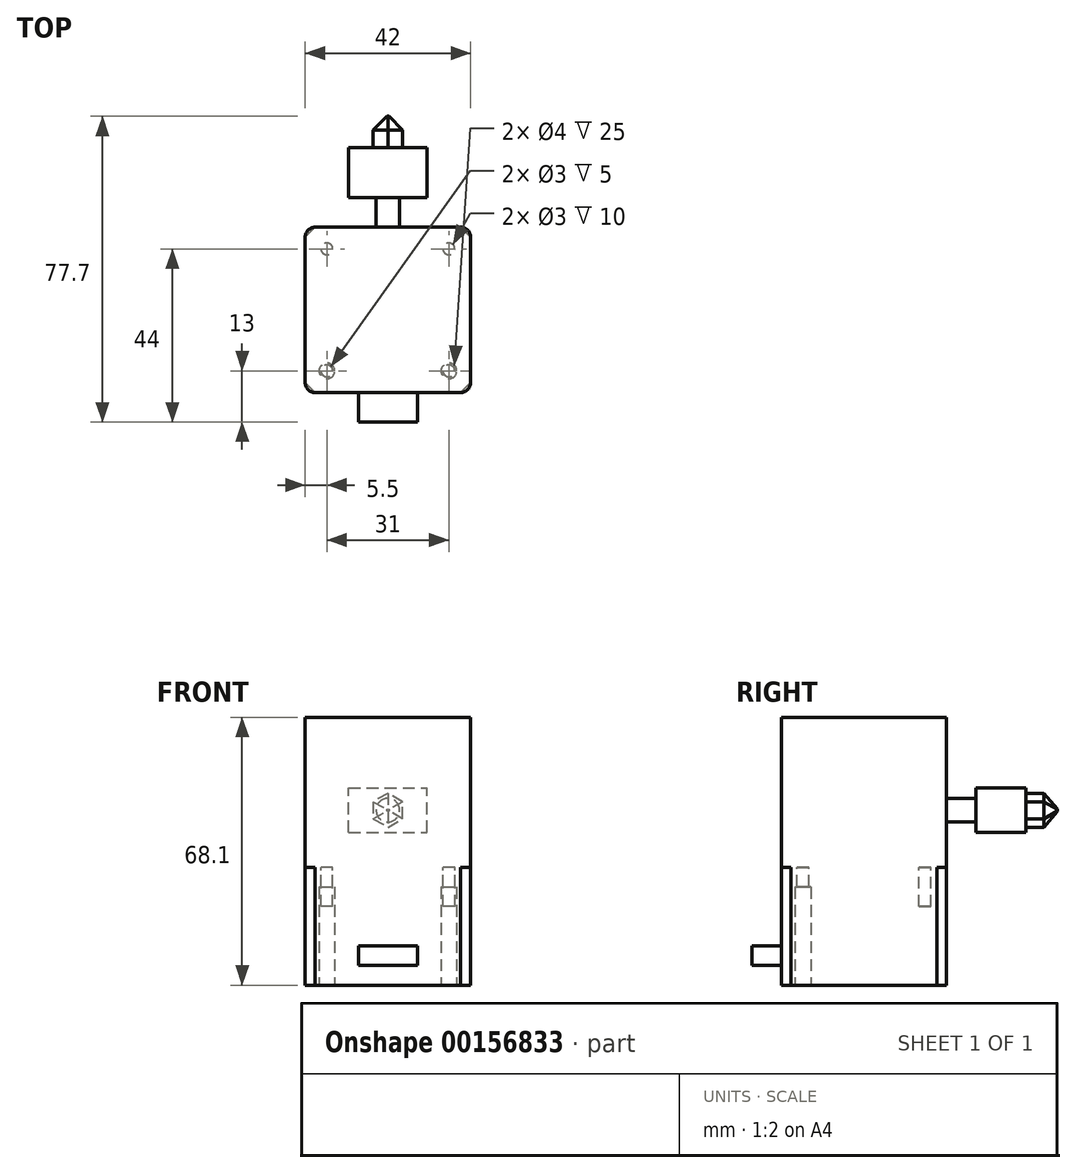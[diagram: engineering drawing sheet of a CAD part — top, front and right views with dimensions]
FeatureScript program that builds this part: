
annotation { "Feature Type Name" : "Feature", "Feature Type Description" : "" }
export const myFeature = defineFeature(function(context is Context, id is Id, definition is map)
    precondition{}
    {
        {
            var Q0;
            Q0=qCreatedBy(makeId("Top.planeOp"),FACE);
            var sketch = newSketch(context, id + "F0", { "sketchPlane" : qUnion([Q0])});
            skLineSegment(sketch, "E0.bottom", {"start": v(21, -21) * mm, "end": v(-21, -21) * mm});
            skLineSegment(sketch, "E0.top", {"start": v(21, 21) * mm, "end": v(-21, 21) * mm});
            skLineSegment(sketch, "E0.left", {"start": v(21, -21) * mm, "end": v(21, 21) * mm});
            skLineSegment(sketch, "E0.right", {"start": v(-21, -21) * mm, "end": v(-21, 21) * mm});
            skPoint(sketch, "E0.middle", {"position": v(0, 0) * mm});
            skSolve(sketch);
        }
        {
            var Q0;
            Q0=qSketchRegion(id+"F0",true);
            extrude(context, id + "F1", {"entities" : qUnion([Q0]), "depth" : 30 * mm});
        }
        {
            var Q0;
            Q0=makeQuery(id+"F1.opExtrude","SWEPT_EDGE",EDGE,{"disambiguationData":[OSD([sQuery(id+"F0.wireOp",EDGE,"E0.bottom"),sQuery(id+"F0.wireOp",EDGE,"E0.right")])]});
            var Q1;
            Q1=makeQuery(id+"F1.opExtrude","SWEPT_EDGE",EDGE,{"disambiguationData":[OSD([sQuery(id+"F0.wireOp",EDGE,"E0.bottom"),sQuery(id+"F0.wireOp",EDGE,"E0.left")])]});
            var Q2;
            Q2=makeQuery(id+"F1.opExtrude","SWEPT_EDGE",EDGE,{"disambiguationData":[OSD([sQuery(id+"F0.wireOp",EDGE,"E0.top"),sQuery(id+"F0.wireOp",EDGE,"E0.left")])]});
            var Q3;
            Q3=makeQuery(id+"F1.opExtrude","SWEPT_EDGE",EDGE,{"disambiguationData":[OSD([sQuery(id+"F0.wireOp",EDGE,"E0.top"),sQuery(id+"F0.wireOp",EDGE,"E0.right")])]});
            chamfer(context, id + "F2", {"entities" : qUnion([Q0, Q1, Q2, Q3]), "width" : 2.5 * mm, "tangentPropagation" : true});
        }
        {
            var Q0;
            Q0=makeQuery(id+"F1.opExtrude","CAP_FACE",FACE,{"disambiguationData":[OSD([sQuery(id+"F0.wireOp",EDGE,"E0.bottom"),sQuery(id+"F0.wireOp",EDGE,"E0.top"),sQuery(id+"F0.wireOp",EDGE,"E0.left"),sQuery(id+"F0.wireOp",EDGE,"E0.right")])],"isStart":false});
            var sketch = newSketch(context, id + "F3", { "sketchPlane" : qUnion([Q0])});
            skLineSegment(sketch, "E1.bottom", {"start": v(15.5, -15.5) * mm, "end": v(-15.5, -15.5) * mm, "construction": true});
            skLineSegment(sketch, "E1.top", {"start": v(15.5, 15.5) * mm, "end": v(-15.5, 15.5) * mm, "construction": true});
            skLineSegment(sketch, "E1.left", {"start": v(15.5, -15.5) * mm, "end": v(15.5, 15.5) * mm, "construction": true});
            skLineSegment(sketch, "E1.right", {"start": v(-15.5, -15.5) * mm, "end": v(-15.5, 15.5) * mm, "construction": true});
            skPoint(sketch, "E1.middle", {"position": v(0, 0) * mm});
            skCircle(sketch, "E2", {"center": v(-15.5, 15.5) * mm, "radius": 1.5 * mm});
            skCircle(sketch, "E3", {"center": v(15.5, 15.5) * mm, "radius": 1.5 * mm});
            skCircle(sketch, "E4", {"center": v(15.5, -15.5) * mm, "radius": 1.5 * mm});
            skCircle(sketch, "E5", {"center": v(-15.5, -15.5) * mm, "radius": 1.5 * mm});
            skSolve(sketch);
        }
        {
            var Q0;
            Q0=qSketchRegion(id+"F3",true);
            extrude(context, id + "F4", {"entities" : qUnion([Q0]), "operationType" : NewBodyOperationType.REMOVE, "oppositeDirection" : true, "depth" : 10 * mm});
        }
        {
            var Q0;
            Q0=makeQuery(id+"F1.opExtrude","CAP_FACE",FACE,{"disambiguationData":[OSD([sQuery(id+"F0.wireOp",EDGE,"E0.bottom"),sQuery(id+"F0.wireOp",EDGE,"E0.top"),sQuery(id+"F0.wireOp",EDGE,"E0.left"),sQuery(id+"F0.wireOp",EDGE,"E0.right")])],"isStart":false});
            var sketch = newSketch(context, id + "F5", { "sketchPlane" : qUnion([Q0])});
            skCircle(sketch, "E6", {"center": v(0, 0) * mm, "radius": 11 * mm});
            skSolve(sketch);
        }
        {
            var Q0;
            Q0=qSketchRegion(id+"F5",true);
            extrude(context, id + "F6", {"entities" : qUnion([Q0]), "operationType" : NewBodyOperationType.ADD, "depth" : 2 * mm});
        }
        {
            var Q0;
            Q0=makeQuery(id+"F6.opExtrude","CAP_FACE",FACE,{"disambiguationData":[OSD([sQuery(id+"F5.wireOp",EDGE,"E6")])],"isStart":false});
            var sketch = newSketch(context, id + "F7", { "sketchPlane" : qUnion([Q0])});
            skArc(sketch, "E7", {"start": v(-2.2, 1.2) * mm, "mid": v(0, -2.5) * mm, "end": v(2.2, 1.2) * mm});
            skLineSegment(sketch, "E8", {"start": v(-2.2, 1.2) * mm, "end": v(2.2, 1.2) * mm});
            skSolve(sketch);
        }
        {
            var Q0;
            Q0=qSketchRegion(id+"F7",true);
            extrude(context, id + "F8", {"entities" : qUnion([Q0]), "operationType" : NewBodyOperationType.ADD, "depth" : 24 * mm});
        }
        {
            var Q0;
            Q0=makeQuery(id+"F1.opExtrude","SWEPT_FACE",FACE,{"disambiguationData":[OSD([sQuery(id+"F0.wireOp",EDGE,"E0.bottom")])]});
            var sketch = newSketch(context, id + "F9", { "sketchPlane" : qUnion([Q0])});
            skLineSegment(sketch, "E9.bottom", {"start": v(7.5, 5) * mm, "end": v(-7.5, 5) * mm});
            skLineSegment(sketch, "E9.top", {"start": v(7.5, 10) * mm, "end": v(-7.5, 10) * mm});
            skLineSegment(sketch, "E9.left", {"start": v(7.5, 5) * mm, "end": v(7.5, 10) * mm});
            skLineSegment(sketch, "E9.right", {"start": v(-7.5, 5) * mm, "end": v(-7.5, 10) * mm});
            skPoint(sketch, "E9.middle", {"position": v(0, 7.5) * mm});
            skSolve(sketch);
        }
        {
            var Q0;
            Q0=qSketchRegion(id+"F9",true);
            extrude(context, id + "F10", {"entities" : qUnion([Q0]), "operationType" : NewBodyOperationType.ADD, "depth" : 7.5 * mm});
        }
        {
            var Q0;
            Q0=makeQuery(id+"F1.opExtrude","CAP_FACE",FACE,{"disambiguationData":[OSD([sQuery(id+"F0.wireOp",EDGE,"E0.bottom"),sQuery(id+"F0.wireOp",EDGE,"E0.top"),sQuery(id+"F0.wireOp",EDGE,"E0.left"),sQuery(id+"F0.wireOp",EDGE,"E0.right")])],"isStart":false});
            var sketch = newSketch(context, id + "F11", { "sketchPlane" : qUnion([Q0])});
            skLineSegment(sketch, "E10.bottom", {"start": v(18.5, -21) * mm, "end": v(-18.5, -21) * mm});
            skLineSegment(sketch, "E10.top", {"start": v(18.5, 21) * mm, "end": v(-18.5, 21) * mm});
            skLineSegment(sketch, "E10.left", {"start": v(21, -18.5) * mm, "end": v(21, 18.5) * mm});
            skLineSegment(sketch, "E10.right", {"start": v(-21, -18.5) * mm, "end": v(-21, 18.5) * mm});
            skPoint(sketch, "E10.middle", {"position": v(0, 0) * mm});
            skPoint(sketch, "E11.visualSharp", {"position": v(-21, 21) * mm});
            skArc(sketch, "E11.filletArc", {"start": v(-18.5, 21) * mm, "mid": v(-20.27, 20.27) * mm, "end": v(-21, 18.5) * mm});
            skPoint(sketch, "E12.visualSharp", {"position": v(21, 21) * mm});
            skArc(sketch, "E12.filletArc", {"start": v(21, 18.5) * mm, "mid": v(20.27, 20.27) * mm, "end": v(18.5, 21) * mm});
            skPoint(sketch, "E13.visualSharp", {"position": v(21, -21) * mm});
            skArc(sketch, "E13.filletArc", {"start": v(18.5, -21) * mm, "mid": v(20.27, -20.27) * mm, "end": v(21, -18.5) * mm});
            skPoint(sketch, "E14.visualSharp", {"position": v(-21, -21) * mm});
            skArc(sketch, "E14.filletArc", {"start": v(-21, -18.5) * mm, "mid": v(-20.27, -20.27) * mm, "end": v(-18.5, -21) * mm});
            skSolve(sketch);
        }
        {
            var Q0;
            Q0=qSketchRegion(id+"F11",true);
            extrude(context, id + "F12", {"entities" : qUnion([Q0]), "operationType" : NewBodyOperationType.ADD, "depth" : 38.1 * mm});
        }
        {
            var Q0;
            Q0=makeQuery(id+"F12.boolean.opBoolean","MERGE",FACE,{"derivedFrom":[makeQuery(id+"F1.opExtrude","SWEPT_FACE",FACE,{"disambiguationData":[OSD([sQuery(id+"F0.wireOp",EDGE,"E0.top")])]}),makeQuery(id+"F12.opExtrude","SWEPT_FACE",FACE,{"disambiguationData":[OSD([sQuery(id+"F11.wireOp",EDGE,"E10.top")])]})]});
            var sketch = newSketch(context, id + "F13", { "sketchPlane" : qUnion([Q0])});
            skCircle(sketch, "E15", {"center": v(0, 44.47) * mm, "radius": 3 * mm});
            skSolve(sketch);
        }
        {
            var Q0;
            Q0=qSketchRegion(id+"F13",true);
            extrude(context, id + "F14", {"entities" : qUnion([Q0]), "operationType" : NewBodyOperationType.ADD, "depth" : 7.5 * mm});
        }
        {
            var Q0;
            Q0=makeQuery(id+"F14.opExtrude","CAP_FACE",FACE,{"disambiguationData":[OSD([sQuery(id+"F13.wireOp",EDGE,"E15")])],"isStart":false});
            var sketch = newSketch(context, id + "F15", { "sketchPlane" : qUnion([Q0])});
            skLineSegment(sketch, "E16.bottom", {"start": v(10, 38.85) * mm, "end": v(-10, 38.85) * mm});
            skLineSegment(sketch, "E16.top", {"start": v(10, 50.1) * mm, "end": v(-10, 50.1) * mm});
            skLineSegment(sketch, "E16.left", {"start": v(10, 38.85) * mm, "end": v(10, 50.1) * mm});
            skLineSegment(sketch, "E16.right", {"start": v(-10, 38.85) * mm, "end": v(-10, 50.1) * mm});
            skPoint(sketch, "E16.middle", {"position": v(0, 44.47) * mm});
            skSolve(sketch);
        }
        {
            var Q0;
            Q0=qSketchRegion(id+"F15",true);
            extrude(context, id + "F16", {"entities" : qUnion([Q0]), "operationType" : NewBodyOperationType.ADD, "depth" : 12.7 * mm});
        }
        {
            var Q0;
            Q0=makeQuery(id+"F16.opExtrude","CAP_FACE",FACE,{"disambiguationData":[OSD([sQuery(id+"F15.wireOp",EDGE,"E16.bottom"),sQuery(id+"F15.wireOp",EDGE,"E16.top"),sQuery(id+"F15.wireOp",EDGE,"E16.left"),sQuery(id+"F15.wireOp",EDGE,"E16.right")])],"isStart":false});
            var sketch = newSketch(context, id + "F17", { "sketchPlane" : qUnion([Q0])});
            skCircle(sketch, "E17.cCircle", {"center": v(0, 44.47) * mm, "radius": 3.75 * mm, "construction": true});
            skPoint(sketch, "E17.cCircle.centerSnap0", {"position": v(0, 50.1) * mm});
            skLineSegment(sketch, "E17.0", {"start": v(3.75, 46.64) * mm, "end": v(3.75, 42.3) * mm});
            skLineSegment(sketch, "E17.1", {"start": v(3.75, 42.3) * mm, "end": v(0, 40.14) * mm});
            skLineSegment(sketch, "E17.2", {"start": v(0, 40.14) * mm, "end": v(-3.75, 42.3) * mm});
            skLineSegment(sketch, "E17.3", {"start": v(-3.75, 42.3) * mm, "end": v(-3.75, 46.64) * mm});
            skLineSegment(sketch, "E17.4", {"start": v(-3.75, 46.64) * mm, "end": v(0, 48.8) * mm});
            skLineSegment(sketch, "E17.5", {"start": v(0, 48.8) * mm, "end": v(3.75, 46.64) * mm});
            skPoint(sketch, "E17.0.midPoint", {"position": v(3.75, 44.47) * mm});
            skSolve(sketch);
        }
        {
            var Q0;
            Q0=qSketchRegion(id+"F17",true);
            extrude(context, id + "F18", {"entities" : qUnion([Q0]), "operationType" : NewBodyOperationType.ADD, "depth" : 8 * mm});
        }
        {
            var Q0;
            Q0=makeQuery(id+"F18.opExtrude","CAP_EDGE",EDGE,{"disambiguationData":[OSD([sQuery(id+"F17.wireOp",EDGE,"E17.1")])],"isStart":false});
            var Q1;
            Q1=makeQuery(id+"F18.opExtrude","CAP_EDGE",EDGE,{"disambiguationData":[OSD([sQuery(id+"F17.wireOp",EDGE,"E17.4")])],"isStart":false});
            var Q2;
            Q2=makeQuery(id+"F18.opExtrude","CAP_EDGE",EDGE,{"disambiguationData":[OSD([sQuery(id+"F17.wireOp",EDGE,"E17.0")])],"isStart":false});
            var Q3;
            Q3=makeQuery(id+"F18.opExtrude","CAP_EDGE",EDGE,{"disambiguationData":[OSD([sQuery(id+"F17.wireOp",EDGE,"E17.2")])],"isStart":false});
            var Q4;
            Q4=makeQuery(id+"F18.opExtrude","CAP_EDGE",EDGE,{"disambiguationData":[OSD([sQuery(id+"F17.wireOp",EDGE,"E17.3")])],"isStart":false});
            var Q5;
            Q5=makeQuery(id+"F18.opExtrude","CAP_EDGE",EDGE,{"disambiguationData":[OSD([sQuery(id+"F17.wireOp",EDGE,"E17.5")])],"isStart":false});
            chamfer(context, id + "F19", {"entities" : qUnion([Q0, Q1, Q2, Q3, Q4, Q5]), "width" : 3.5 * mm, "tangentPropagation" : true});
        }
        {
            var Q0;
            Q0=makeQuery(id+"F1.opExtrude","CAP_FACE",FACE,{"disambiguationData":[OSD([sQuery(id+"F0.wireOp",EDGE,"E0.bottom"),sQuery(id+"F0.wireOp",EDGE,"E0.top"),sQuery(id+"F0.wireOp",EDGE,"E0.left"),sQuery(id+"F0.wireOp",EDGE,"E0.right")])],"isStart":true});
            var sketch = newSketch(context, id + "F20", { "sketchPlane" : qUnion([Q0])});
            skLineSegment(sketch, "E18.bottom", {"start": v(15.5, -15.5) * mm, "end": v(-15.5, -15.5) * mm, "construction": true});
            skLineSegment(sketch, "E18.top", {"start": v(15.5, 15.5) * mm, "end": v(-15.5, 15.5) * mm, "construction": true});
            skLineSegment(sketch, "E18.left", {"start": v(15.5, -15.5) * mm, "end": v(15.5, 15.5) * mm, "construction": true});
            skLineSegment(sketch, "E18.right", {"start": v(-15.5, -15.5) * mm, "end": v(-15.5, 15.5) * mm, "construction": true});
            skPoint(sketch, "E18.middle", {"position": v(0, 0) * mm});
            skCircle(sketch, "E19", {"center": v(-15.5, 15.5) * mm, "radius": 2 * mm});
            skCircle(sketch, "E20", {"center": v(15.5, 15.5) * mm, "radius": 2 * mm});
            skSolve(sketch);
        }
        {
            var Q0;
            Q0=qSketchRegion(id+"F20",true);
            extrude(context, id + "F21", {"entities" : qUnion([Q0]), "operationType" : NewBodyOperationType.REMOVE, "oppositeDirection" : true, "depth" : 25 * mm});
        }
    });
